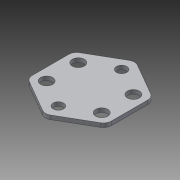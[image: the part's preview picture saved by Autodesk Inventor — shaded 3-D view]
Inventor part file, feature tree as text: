
AUTODESK INVENTOR PART (.ipt)
format: ipt  version: 2014 SP1 (Build 180222100, 222)  size: 114,176 bytes
history: native  units: in
note: dims shown in document units (in); Inventor stores cm internally (conversion verified against a paired STEP export)
features: extrude x1, sketch x1
ambient origin geometry x8: Origin, YZ Plane, XZ Plane, XY Plane, X Axis, Y Axis, Z Axis, Center Point
bodies: Solid1 (feature_tree)
feature tree (2):
  extrude  "Extrusion1"  Depth=0.0625in
  sketch  "Sketch1"  dims[d0=0.164in d1=0.164in d2=1.0in d3=0.19in d4=0.19in d5=0.5in d6=0.435in d7=0.435in d8=0.25in d9=0.19in d10=0.19in d11=0.435in d12=0.5in d13=1.25in d14=0.125in d15=0.0625in d16=0.0in]
